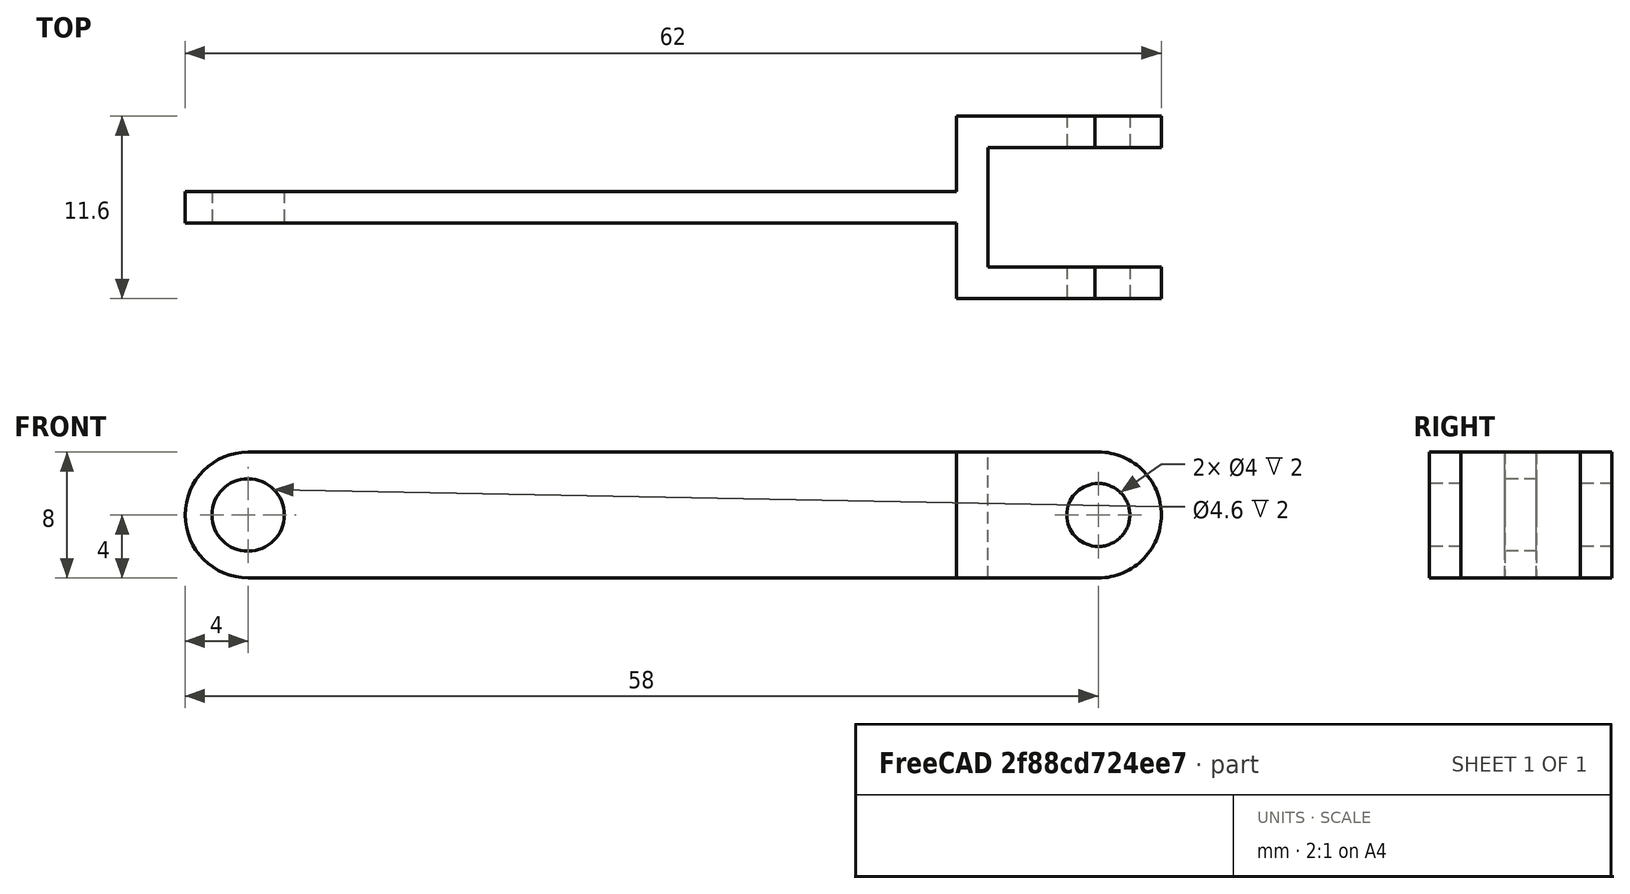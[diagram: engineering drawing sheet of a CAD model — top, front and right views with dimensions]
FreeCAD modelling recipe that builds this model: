
FCSTD DOCUMENT  (FreeCAD 0.18R16110 (Git))
Label: group
License: All rights reserved
LicenseURL: http://en.wikipedia.org/wiki/All_rights_reserved
objects: TechDraw::DrawViewDimension×7, Part::Cylinder×6, Part::Box×4, Part::MultiFuse×4, TechDraw::DrawProjGroupItem×4, Part::Cut×3, TechDraw::DrawSVGTemplate×2, TechDraw::DrawPage×2, TechDraw::DrawViewPart×1, TechDraw::DrawProjGroup×1
note: 17 computed .brp shape members not serialized (recipe doc carries the construction recipe); baked Part::Feature solids carry a one-line shape summary decoded from their .brp

FEATURE [Part::Box] Box  label="Cube"
  AttacherType = Attacher::AttachEngine3D
  Height = 8
  Length = 45
  Width = 2
FEATURE [Part::Cylinder] Cylinder
  Angle = 360
  AttacherType = Attacher::AttachEngine3D
  Height = 2
  Placement = pos=(0,0,4) rot=(-1,0,0;1.5708rad)
  Radius = 4
FEATURE [Part::Cylinder] Cylinder001
  Angle = 360
  AttacherType = Attacher::AttachEngine3D
  Height = 2
  Placement = pos=(0,2,4) rot=(1,0,0;1.5708rad)
  Radius = 2.3
FEATURE [Part::MultiFuse] Fusion
  Shapes = -> [Box,Cylinder]
FEATURE [Part::Cut] Cut
  Base = -> Fusion
  Tool = -> Cylinder001
FEATURE [Part::Box] Box001  label="Cube001"
  AttacherType = Attacher::AttachEngine3D
  Height = 8
  Length = 2
  Placement = pos=(45,-4.8,0) rot=(0,0,1;0rad)
  Width = 11.6
FEATURE [Part::Box] Box002  label="Cube002"
  AttacherType = Attacher::AttachEngine3D
  Height = 8
  Length = 6.8
  Placement = pos=(47,4.8,0) rot=(0,0,1;0rad)
  Width = 2
FEATURE [Part::Cylinder] Cylinder002
  Angle = 360
  AttacherType = Attacher::AttachEngine3D
  Height = 2
  Placement = pos=(54,6.8,4) rot=(1,0,0;1.5708rad)
  Radius = 4
FEATURE [Part::MultiFuse] Fusion001
  Shapes = -> [Cylinder002,Box002]
FEATURE [Part::Cylinder] Cylinder003
  Angle = 360
  AttacherType = Attacher::AttachEngine3D
  Height = 2
  Placement = pos=(54,6.8,4) rot=(1,0,0;1.5708rad)
  Radius = 2
FEATURE [Part::Cut] Cut001
  Base = -> Fusion001
  Tool = -> Cylinder003
FEATURE [Part::Cylinder] Cylinder004
  Angle = 360
  AttacherType = Attacher::AttachEngine3D
  Height = 2
  Placement = pos=(54,6.8,4) rot=(1,0,0;1.5708rad)
  Radius = 4
FEATURE [Part::Cylinder] Cylinder005
  Angle = 360
  AttacherType = Attacher::AttachEngine3D
  Height = 2
  Placement = pos=(54,6.8,4) rot=(1,0,0;1.5708rad)
  Radius = 2
FEATURE [Part::Box] Box003  label="Cube003"
  AttacherType = Attacher::AttachEngine3D
  Height = 8
  Length = 6.8
  Placement = pos=(47,4.8,0) rot=(0,0,1;0rad)
  Width = 2
FEATURE [Part::MultiFuse] Fusion002
  Shapes = -> [Cylinder004,Box003]
FEATURE [Part::Cut] Cut002
  Base = -> Fusion002
  Placement = pos=(0,-9.6,0) rot=(0,0,1;0rad)
  Tool = -> Cylinder005
FEATURE [Part::MultiFuse] Fusion003
  Shapes = -> [Box001,Cut001,Cut,Cut002]
FEATURE [TechDraw::DrawSVGTemplate] Template
  EditableTexts = Designed_by_Name=Designed by Name; Drawing_number=Drawing number; FC-Date=Date; FC-SC=Scale; FC-SH=Sheet; FC-Title=Title; Subtitle=Subtitle; Weight=Weight
  Height = 210
  Orientation = 1
  Width = 297
FEATURE [TechDraw::DrawViewPart] View
  CoarseView = false
  Direction = (0,-1,0)
  Focus = 100
  HardHidden = false
  IsoCount = 0
  IsoHidden = false
  IsoVisible = false
  LockPosition = false
  Perspective = false
  Rotation = 0
  ScaleType = 0
  SeamHidden = false
  SeamVisible = false
  SmoothHidden = false
  SmoothVisible = false
  Source = -> [Fusion003]
  X = 148.5
  Y = 105
FEATURE [TechDraw::DrawPage] Page
  KeepUpdated = true
  ProjectionType = 0
  Template = -> Template
  Views = -> [View]
FEATURE [TechDraw::DrawSVGTemplate] Template001
  EditableTexts = Approved1=Approved 1; Approved2=Approved 2; CheckedBy=Checked By; Code=Code; CompanyAddress=1234 Main St; CompanyName=Company Name; DrawingNumber=Drawing Number; DrawingTitle1=Arm piston; DrawingTitle2=Drawing Title 2; DrawingTitle3=Drawing Title 3; DrawnBy=Drawn By; Revision=Rev; Scale=Scale; Sheet=Sheet n of m; Weight=Weight
  Height = 279.4
  Orientation = 1
  Width = 431.8
FEATURE [TechDraw::DrawProjGroupItem] ProjItem  label="Front"
  CoarseView = false
  Direction = (0,-1,0)
  Focus = 100
  HardHidden = false
  IsoCount = 0
  IsoHidden = false
  IsoVisible = false
  LockPosition = true
  Perspective = false
  Rotation = 0
  RotationVector = (1,0,0)
  Scale = 2
  ScaleType = 2
  SeamHidden = false
  SeamVisible = false
  SmoothHidden = false
  SmoothVisible = false
  Source = -> [Fusion003]
  Type = 0
  X = 0
  Y = 0
FEATURE [TechDraw::DrawProjGroupItem] ProjItem001  label="Left"
  CoarseView = false
  Direction = (-1,-1e-16,0)
  Focus = 100
  HardHidden = false
  IsoCount = 0
  IsoHidden = false
  IsoVisible = false
  LockPosition = false
  Perspective = false
  Rotation = 0
  RotationVector = (1e-16,-1,0)
  Scale = 2
  ScaleType = 2
  SeamHidden = false
  SeamVisible = false
  SmoothHidden = false
  SmoothVisible = false
  Source = -> [Fusion003]
  Type = 1
  X = 139
  Y = 0
FEATURE [TechDraw::DrawProjGroupItem] ProjItem002  label="FrontTopLeft"
  CoarseView = false
  Direction = (-1,-1,1)
  Focus = 100
  HardHidden = false
  IsoCount = 0
  IsoHidden = false
  IsoVisible = false
  LockPosition = false
  Perspective = false
  Rotation = 0
  RotationVector = (1,-1,0)
  Scale = 2
  ScaleType = 2
  SeamHidden = false
  SeamVisible = false
  SmoothHidden = false
  SmoothVisible = false
  Source = -> [Fusion003]
  Type = 6
  X = 139
  Y = -139
FEATURE [TechDraw::DrawProjGroupItem] ProjItem003  label="Top"
  CoarseView = false
  Direction = (0,0,1)
  Focus = 100
  HardHidden = false
  IsoCount = 0
  IsoHidden = false
  IsoVisible = false
  LockPosition = false
  Perspective = false
  Rotation = 0
  RotationVector = (1,0,0)
  Scale = 2
  ScaleType = 2
  SeamHidden = false
  SeamVisible = false
  SmoothHidden = false
  SmoothVisible = false
  Source = -> [Fusion003]
  Type = 4
  X = 0
  Y = -139
FEATURE [TechDraw::DrawProjGroup] ProjGroup
  Anchor = -> ProjItem
  AutoDistribute = true
  LockPosition = false
  ProjectionType = 0
  Rotation = 0
  Scale = 2
  ScaleType = 2
  Source = -> [Fusion003]
  Views = -> [ProjItem,ProjItem001,ProjItem002,ProjItem003]
  X = 113.121
  Y = 233.166
  spacingX = 15
  spacingY = 15
FEATURE [TechDraw::DrawViewDimension] Dimension
  Arbitrary = false
  FormatSpec = %.2f
  LockPosition = false
  MeasureType = 1
  OverTolerance = 0
  References2D = -> [ProjItem003]
  Rotation = 0
  ScaleType = 0
  Type = 1
  UnderTolerance = 0
  X = -9
  Y = -2
FEATURE [TechDraw::DrawViewDimension] Dimension001
  Arbitrary = false
  FormatSpec = %.2f
  LockPosition = false
  MeasureType = 1
  OverTolerance = 0
  References2D = -> [ProjItem003]
  Rotation = 0
  ScaleType = 0
  Type = 1
  UnderTolerance = 0
  X = -58
  Y = -2
FEATURE [TechDraw::DrawViewDimension] Dimension002
  Arbitrary = false
  FormatSpec = %.2f
  LockPosition = false
  MeasureType = 1
  OverTolerance = 0
  References2D = -> [ProjItem003]
  Rotation = 0
  ScaleType = 0
  Type = 1
  UnderTolerance = 0
  X = 46.8
  Y = 11.6
FEATURE [TechDraw::DrawViewDimension] Dimension003
  Arbitrary = false
  FormatSpec = %.2f
  LockPosition = false
  MeasureType = 1
  OverTolerance = 0
  References2D = -> [ProjItem003]
  Rotation = 0
  ScaleType = 0
  Type = 1
  UnderTolerance = 0
  X = 57.8
  Y = 11.6
FEATURE [TechDraw::DrawViewDimension] Dimension004
  Arbitrary = false
  FormatSpec = %.2f
  LockPosition = false
  MeasureType = 1
  OverTolerance = 0
  References2D = -> [ProjItem003]
  Rotation = 0
  ScaleType = 0
  Type = 1
  UnderTolerance = 0
  X = 38
  Y = -11.6
FEATURE [TechDraw::DrawViewDimension] Dimension005
  Arbitrary = false
  FormatSpec = %.2f
  LockPosition = false
  MeasureType = 1
  OverTolerance = 0
  References2D = -> [ProjItem001]
  Rotation = 0
  ScaleType = 0
  Type = 2
  UnderTolerance = 0
  X = 11.6
  Y = 0
FEATURE [TechDraw::DrawViewDimension] Dimension006
  Arbitrary = false
  FormatSpec = %.2f
  LockPosition = false
  MeasureType = 1
  OverTolerance = 0
  References2D = -> [ProjItem003]
  Rotation = 0
  ScaleType = 0
  Type = 2
  UnderTolerance = 0
  X = 36
  Y = -6.8
FEATURE [TechDraw::DrawPage] Page001
  KeepUpdated = true
  ProjectionType = 0
  Template = -> Template001
  Views = -> [ProjGroup,Dimension,Dimension001,Dimension002,Dimension003,Dimension004,Dimension005,Dimension006]
